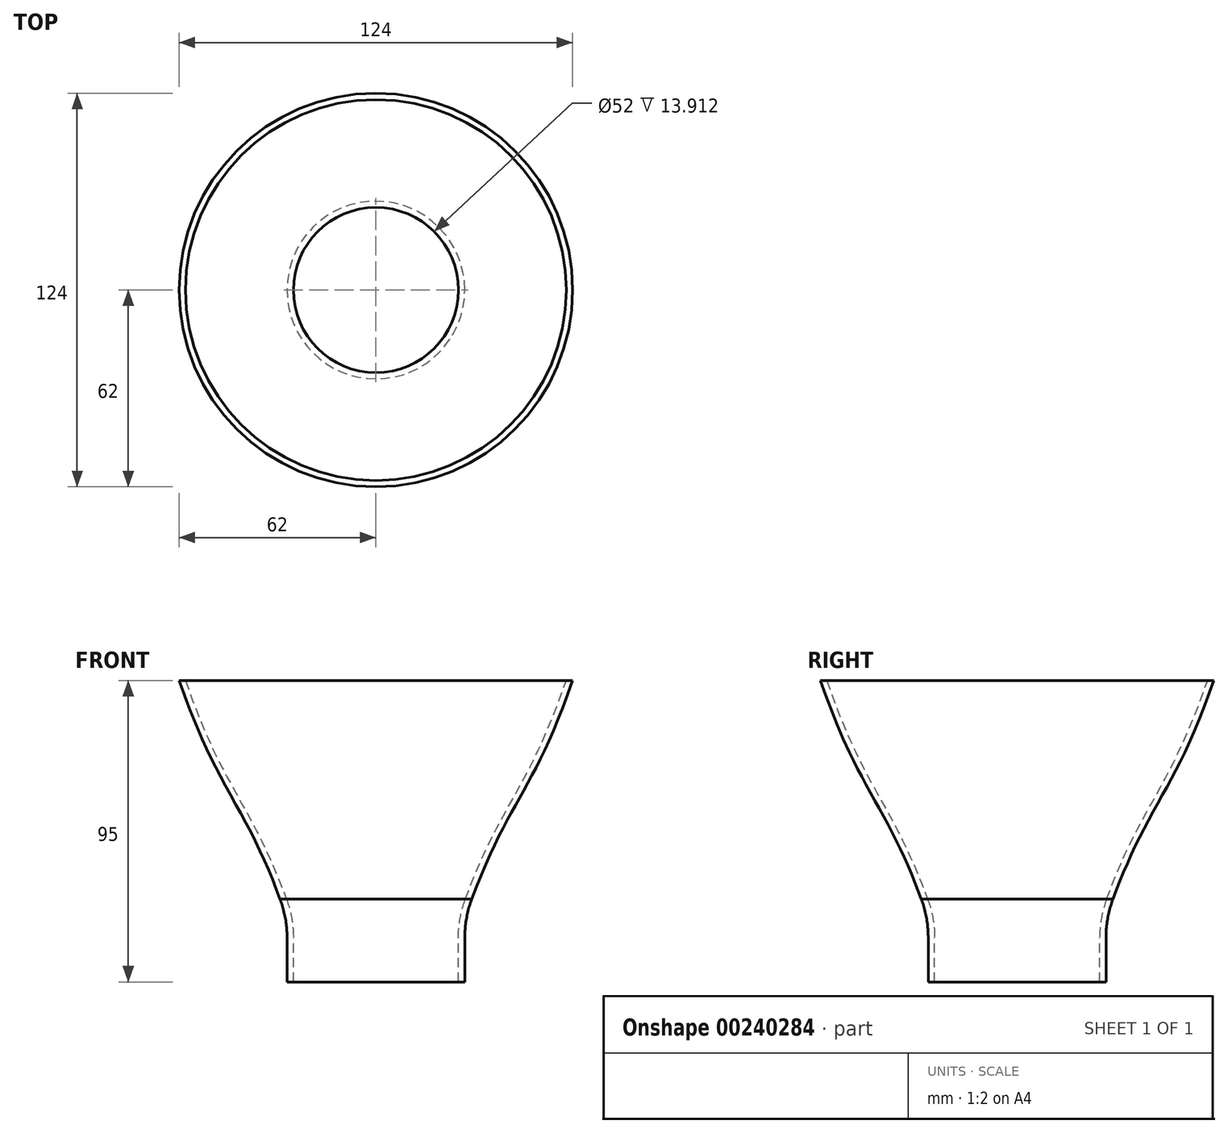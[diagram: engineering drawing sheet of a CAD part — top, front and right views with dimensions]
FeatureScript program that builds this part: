
annotation { "Feature Type Name" : "Feature", "Feature Type Description" : "" }
export const myFeature = defineFeature(function(context is Context, id is Id, definition is map)
    precondition{}
    {
        {
            var Q0;
            Q0=qCreatedBy(makeId("Front.planeOp"),FACE);
            var sketch = newSketch(context, id + "F0", { "sketchPlane" : qUnion([Q0])});
            skLineSegment(sketch, "E0", {"start": v(0, 0) * mm, "end": v(60, 0) * mm, "construction": true});
            skLineSegment(sketch, "E1", {"start": v(0, 0) * mm, "end": v(0, -75) * mm, "construction": true});
            skLineSegment(sketch, "E2", {"start": v(0, -75) * mm, "end": v(26, -75) * mm, "construction": true});
            skLineSegment(sketch, "E3", {"start": v(26, -75) * mm, "end": v(28, -75) * mm});
            skLineSegment(sketch, "E4", {"start": v(60, 0) * mm, "end": v(62, 0) * mm});
            skLineSegment(sketch, "E5", {"start": v(0, -37.5) * mm, "end": v(64.59, -37.5) * mm, "construction": true});
            skLineSegment(sketch, "E6", {"start": v(60, 0) * mm, "end": v(26, -75) * mm, "construction": true});
            skLineSegment(sketch, "E7", {"start": v(62, 0) * mm, "end": v(28, -75) * mm, "construction": true});
            skFitSpline(sketch, "E8", {"points": [v(26, -75) * mm, v(43, -37.5) * mm, v(60, 0) * mm], "startDerivative": vector(39, 112.5) * mm, "endDerivative": vector(39, 112.5) * mm});
            skPoint(sketch, "E9", {"position": v(45, -37.5) * mm});
            skPoint(sketch, "E10", {"position": v(62, 0) * mm});
            skPoint(sketch, "E11", {"position": v(28, -75) * mm});
            skPoint(sketch, "E12", {"position": v(36.5, -56.25) * mm});
            skLineSegment(sketch, "E13", {"start": v(58, 0) * mm, "end": v(24, -75) * mm, "construction": true});
            skPoint(sketch, "E14", {"position": v(49.5, -18.75) * mm});
            skPoint(sketch, "E15", {"position": v(41, -37.5) * mm});
            skFitSpline(sketch, "E16", {"points": [v(28, -75) * mm, v(45, -37.5) * mm, v(62, 0) * mm], "startDerivative": vector(39, 112.5) * mm, "endDerivative": vector(39, 112.5) * mm});
            skLineSegment(sketch, "E17", {"start": v(62, 0) * mm, "end": v(64, 0) * mm, "construction": true});
            skLineSegment(sketch, "E18", {"start": v(64, 0) * mm, "end": v(30, -75) * mm, "construction": true});
            skLineSegment(sketch, "E19", {"start": v(30, -75) * mm, "end": v(28, -75) * mm, "construction": true});
            skPoint(sketch, "E20", {"position": v(47, -37.5) * mm});
            skSolve(sketch);
        }
        {
            var Q0;
            Q0 = qSketchRegion(id + "F0", true);
            var Q1;
            Q1=sQuery(id+"F0.wireOp",EDGE,"E1");
            revolve(context, id + "F1", {"entities" : qUnion([Q0]), "axis" : qUnion([Q1]), "revolveType" : RevolveType.FULL});
        }
        {
            var Q0;
            Q0=makeQuery(id+"F1.opRevolve","SWEPT_FACE",FACE,{"disambiguationData":[OSD([sQuery(id+"F0.wireOp",EDGE,"E3")])]});
            var sketch = newSketch(context, id + "F2", { "sketchPlane" : qUnion([Q0])});
            skSolve(sketch);
        }
        {
            var Q0;
            {var subQ0=sQuery(id+"F0.wireOp",EDGE,"E3");Q0=makeQuery(id+"F2.imprint","IMPRINT",FACE,{"disambiguationData":[TD([[makeQuery(id+"F2.imprint","IMPRINT",EDGE,{"derivedFrom":makeQuery(id+"F1.opRevolve","SWEPT_EDGE",EDGE,{"disambiguationData":[OSD([sQuery(id+"F0.wireOp",EDGE,"d2e3f0ac-cd2f-4c4a-92f9-76ff8c2d9be3"),subQ0])]})}),1.0]])]});}
            extrude(context, id + "F3", {"entities" : qUnion([Q0]), "operationType" : NewBodyOperationType.ADD, "depth" : 20 * mm});
        }
        {
            var Q0;
            {var subQ0=sQuery(id+"F0.wireOp",EDGE,"E3");var subQ1=sQuery(id+"F0.wireOp",EDGE,"13e73789-7f5c-457e-8921-e15cbbe864b0");Q0=makeQuery(id+"F3.boolean.opBoolean","MERGE",EDGE,{"derivedFrom":[makeQuery(id+"F1.opRevolve","SWEPT_EDGE",EDGE,{"disambiguationData":[OSD([subQ1,subQ0])]}),makeQuery(id+"F3.opExtrude","CAP_EDGE",EDGE,{"disambiguationData":[OSD([subQ1,subQ0])],"isStart":true})]});}
            fillet(context, id + "F4", {"entities" : qUnion([Q0]), "radius" : 35 * mm, "tangentPropagation" : true, "allowEdgeOverflow" : false});
        }
    });
